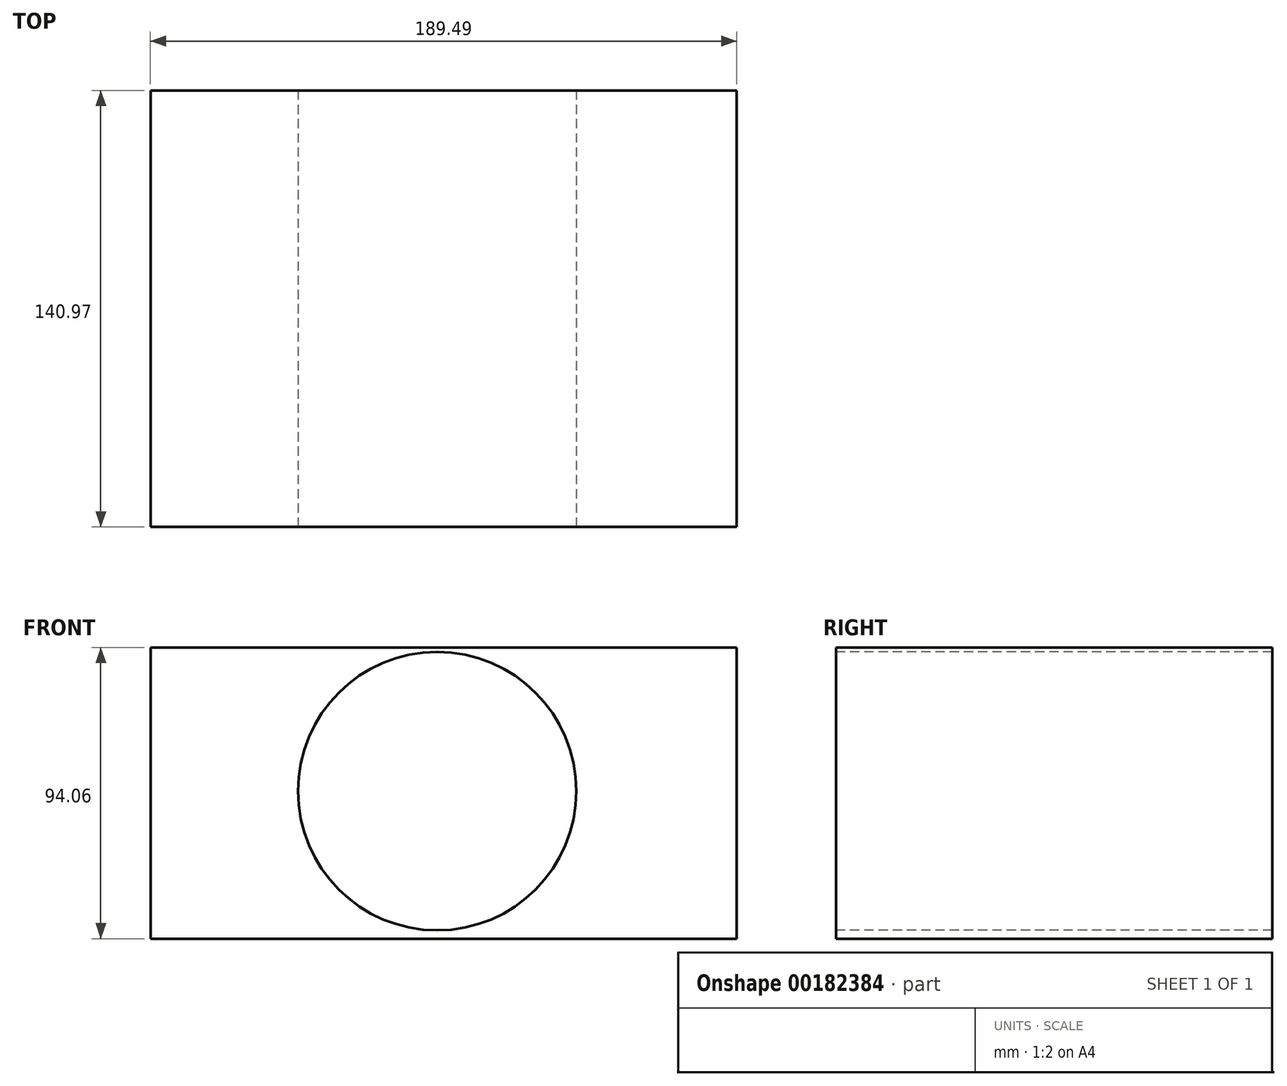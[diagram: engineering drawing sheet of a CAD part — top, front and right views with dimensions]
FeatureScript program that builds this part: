
annotation { "Feature Type Name" : "Feature", "Feature Type Description" : "" }
export const myFeature = defineFeature(function(context is Context, id is Id, definition is map)
    precondition{}
    {
        {
            var Q0;
            Q0=qCreatedBy(makeId("Front.planeOp"),FACE);
            var sketch = newSketch(context, id + "F0", { "sketchPlane" : qUnion([Q0])});
            skLineSegment(sketch, "E0.bottom", {"start": v(49.6, -47.03) * mm, "end": v(-49.6, -47.03) * mm});
            skLineSegment(sketch, "E0.top", {"start": v(49.6, 47.03) * mm, "end": v(-49.6, 47.03) * mm});
            skLineSegment(sketch, "E0.left", {"start": v(49.6, -47.03) * mm, "end": v(49.6, 47.03) * mm});
            skLineSegment(sketch, "E0.right", {"start": v(-49.6, -47.03) * mm, "end": v(-49.6, 47.03) * mm});
            skPoint(sketch, "E0.middle", {"position": v(0, 0) * mm});
            skSolve(sketch);
        }
        {
            var Q0;
            Q0=makeQuery(id+"F0.imprint","IMPRINT",FACE,{"disambiguationData":[TD([[makeQuery(id+"F0.imprint","IMPRINT",EDGE,{"derivedFrom":sQuery(id+"F0.wireOp",EDGE,"E0.bottom")}),-1.0]])]});
            var Q1;
            Q1=sQuery(id+"F0.wireOp",EDGE,"E0.right");
            var Q2;
            Q2=sQuery(id+"F0.wireOp",EDGE,"E0.left");
            var Q3;
            Q3=sQuery(id+"F0.wireOp",EDGE,"E0.top");
            var Q4;
            Q4=sQuery(id+"F0.wireOp",EDGE,"E0.bottom");
            extrude(context, id + "F1", {"entities" : qUnion([Q0]), "bodyType" : ToolBodyType.SURFACE, "operationType" : NewBodyOperationType.ADD, "surfaceEntities" : qUnion([Q1, Q2, Q3, Q4]), "endBound" : BoundingType.SYMMETRIC, "depth" : 280.92 * mm});
        }
        {
            var Q0;
            Q0=makeQuery(id+"F1.opExtrude","SWEPT_FACE",FACE,{"disambiguationData":[OSD([sQuery(id+"F0.wireOp",EDGE,"E0.left")])]});
            extrude(context, id + "F2", {"entities" : qUnion([Q0]), "depth" : 189.48 * mm});
        }
        {
            var Q0;
            {var subQ0=sQuery(id+"F0.wireOp",EDGE,"E0.left");Q0=makeQuery(id+"F2.opExtrude","SWEPT_FACE",FACE,{"disambiguationData":[OSD([subQ0]),TDD([makeQuery(id+"F1.opExtrude","CAP_EDGE",EDGE,{"disambiguationData":[OSD([subQ0])],"isStart":false})])]});}
            extrude(context, id + "F3", {"entities" : qUnion([Q0]), "operationType" : NewBodyOperationType.REMOVE, "oppositeDirection" : true, "depth" : 139.95 * mm});
        }
        {
            var Q0;
            Q0=makeQuery(id+"F3.boolean.opBoolean","COPY",FACE,{"derivedFrom":makeQuery(id+"F3.opExtrude","CAP_FACE",FACE,{"disambiguationData":[OSD([sQuery(id+"F0.wireOp",EDGE,"E0.left")])],"isStart":false})});
            var sketch = newSketch(context, id + "F4", { "sketchPlane" : qUnion([Q0])});
            skCircle(sketch, "E1", {"center": v(142.25, 0.65) * mm, "radius": 44.98 * mm});
            skPoint(sketch, "E1.first.point", {"position": v(100.6, 17.64) * mm});
            skPoint(sketch, "E1.second.point", {"position": v(185.3, -12.36) * mm});
            skPoint(sketch, "E1.third.point", {"position": v(177.8, 28.19) * mm});
            skSolve(sketch);
        }
        {
            var Q0;
            Q0=makeQuery(id+"F4.imprint","IMPRINT",FACE,{"disambiguationData":[TD([[makeQuery(id+"F4.imprint","IMPRINT",EDGE,{"derivedFrom":sQuery(id+"F4.wireOp",EDGE,"E1")}),1.0]])]});
            extrude(context, id + "F5", {"entities" : qUnion([Q0]), "operationType" : NewBodyOperationType.REMOVE, "oppositeDirection" : true, "depth" : 142.24 * mm});
        }
    });
